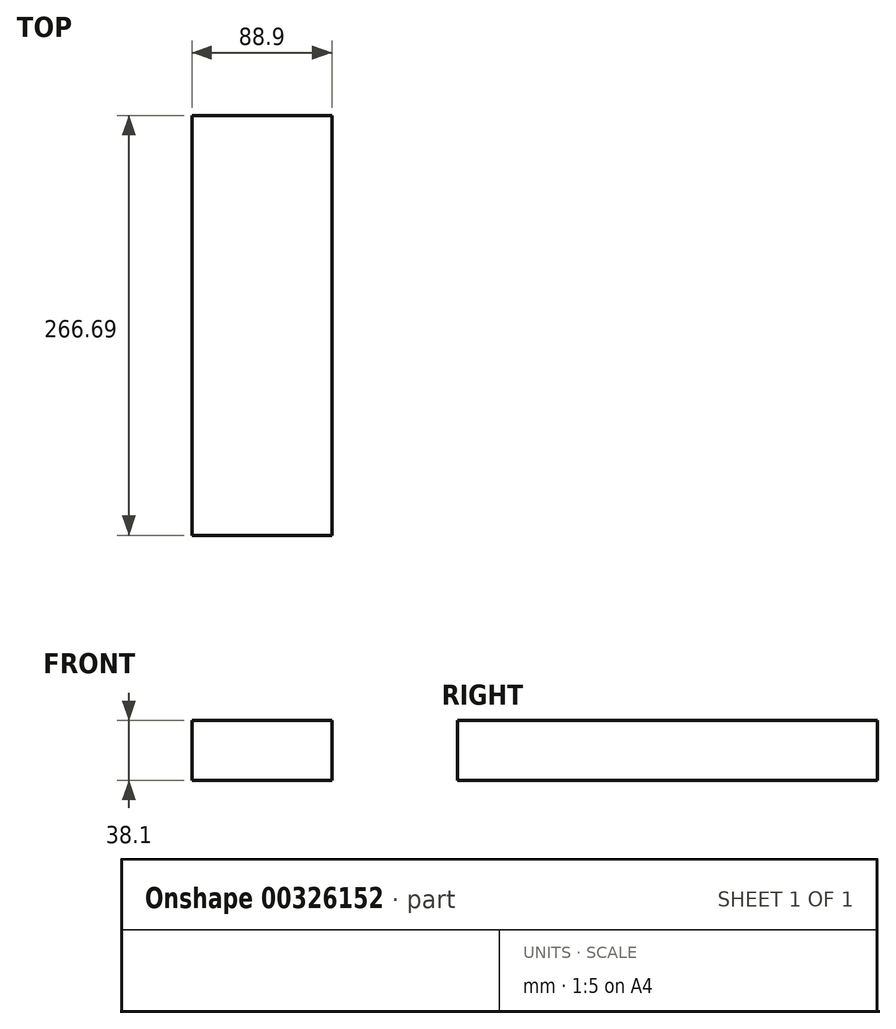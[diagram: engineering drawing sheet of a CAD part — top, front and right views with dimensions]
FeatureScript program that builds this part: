
annotation { "Feature Type Name" : "Feature", "Feature Type Description" : "" }
export const myFeature = defineFeature(function(context is Context, id is Id, definition is map)
    precondition{}
    {
        {
            var Q0;
            Q0=qCreatedBy(makeId("Right.planeOp"),FACE);
            var sketch = newSketch(context, id + "F0", { "sketchPlane" : qUnion([Q0])});
            skLineSegment(sketch, "E0.bottom", {"start": v(60.44, 0) * mm, "end": v(-75.7, 0) * mm});
            skLineSegment(sketch, "E0.top", {"start": v(60.44, 35.3) * mm, "end": v(-75.7, 35.3) * mm});
            skLineSegment(sketch, "E0.left", {"start": v(60.44, 0) * mm, "end": v(60.44, 35.3) * mm});
            skLineSegment(sketch, "E0.right", {"start": v(-75.7, 0) * mm, "end": v(-75.7, 35.3) * mm});
            skSolve(sketch);
        }
        {
            var Q0;
            Q0=makeQuery(id+"F0.imprint","IMPRINT",FACE,{"disambiguationData":[TD([[makeQuery(id+"F0.imprint","IMPRINT",EDGE,{"derivedFrom":sQuery(id+"F0.wireOp",EDGE,"E0.bottom")}),-1.0]])]});
            extrude(context, id + "F1", {"entities" : qUnion([Q0]), "depth" : 88.9 * mm});
        }
        {
            var Q0;
            Q0=makeQuery(id+"F1.opExtrude","SWEPT_FACE",FACE,{"disambiguationData":[OSD([sQuery(id+"F0.wireOp",EDGE,"E0.top")])]});
            extrude(context, id + "F2", {"entities" : qUnion([Q0]), "operationType" : NewBodyOperationType.ADD, "depth" : 2.8 * mm});
        }
        {
            var Q0;
            {var subQ0=sQuery(id+"F0.wireOp",EDGE,"E0.right");Q0=makeQuery(id+"F2.boolean.opBoolean","MERGE",FACE,{"derivedFrom":[makeQuery(id+"F1.opExtrude","SWEPT_FACE",FACE,{"disambiguationData":[OSD([subQ0])]}),makeQuery(id+"F2.opExtrude","SWEPT_FACE",FACE,{"disambiguationData":[OSD([sQuery(id+"F0.wireOp",EDGE,"E0.top"),subQ0])]})]});}
            extrude(context, id + "F3", {"entities" : qUnion([Q0]), "operationType" : NewBodyOperationType.ADD, "depth" : 130.56 * mm});
        }
    });
